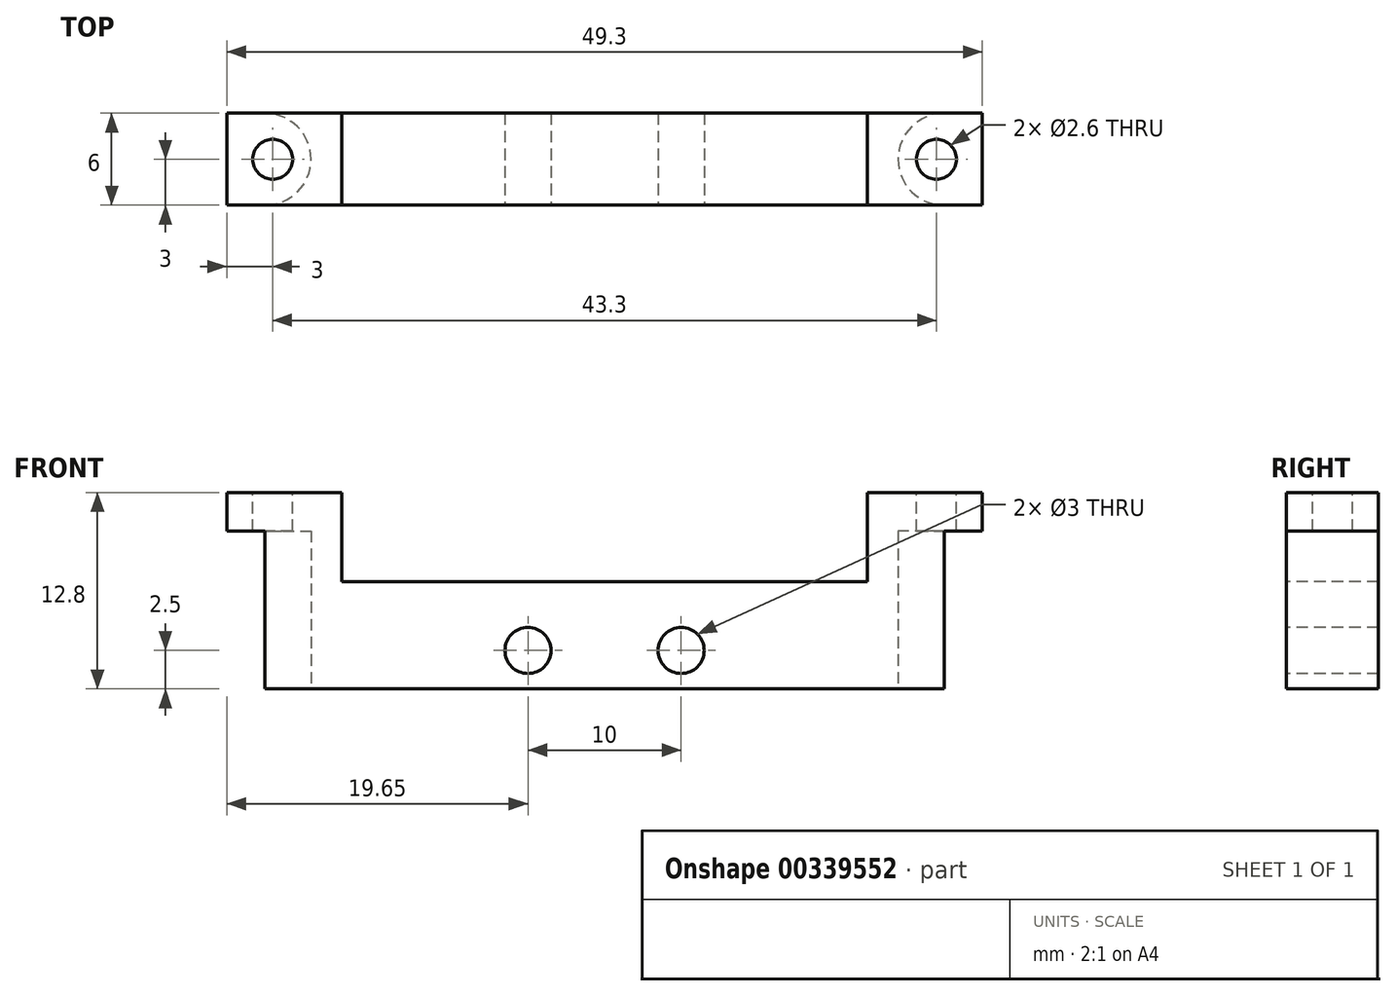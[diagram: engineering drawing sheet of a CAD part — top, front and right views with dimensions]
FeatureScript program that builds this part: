
annotation { "Feature Type Name" : "Feature", "Feature Type Description" : "" }
export const myFeature = defineFeature(function(context is Context, id is Id, definition is map)
    precondition{}
    {
        {
            var Q0;
            Q0=qCreatedBy(makeId("Top.planeOp"),FACE);
            var sketch = newSketch(context, id + "F0", { "sketchPlane" : qUnion([Q0])});
            skLineSegment(sketch, "E0.bottom", {"start": v(0, 3) * mm, "end": v(-24.65, 3) * mm});
            skLineSegment(sketch, "E0.top", {"start": v(0, -3) * mm, "end": v(-24.65, -3) * mm});
            skLineSegment(sketch, "E0.left", {"start": v(0, 3) * mm, "end": v(0, -3) * mm});
            skLineSegment(sketch, "E0.right", {"start": v(-24.65, 3) * mm, "end": v(-24.65, -3) * mm});
            skSolve(sketch);
        }
        {
            var Q0;
            Q0=makeQuery(id+"F0.imprint","IMPRINT",FACE,{"disambiguationData":[TD([[makeQuery(id+"F0.imprint","IMPRINT",EDGE,{"derivedFrom":sQuery(id+"F0.wireOp",EDGE,"E0.bottom")}),1.0]])]});
            extrude(context, id + "F1", {"entities" : qUnion([Q0]), "depth" : (10.3 + 2.5) * mm});
        }
        {
            var Q0;
            Q0=makeQuery(id+"F1.opExtrude","SWEPT_FACE",FACE,{"disambiguationData":[OSD([sQuery(id+"F0.wireOp",EDGE,"E0.top")])]});
            var sketch = newSketch(context, id + "F2", { "sketchPlane" : qUnion([Q0])});
            skLineSegment(sketch, "E1", {"start": v(-17.15, 12.8) * mm, "end": v(-17.15, 7) * mm});
            skLineSegment(sketch, "E2", {"start": v(-17.15, 7) * mm, "end": v(0, 7) * mm});
            skLineSegment(sketch, "E3", {"start": v(-17.15, 12.8) * mm, "end": v(0, 12.8) * mm});
            skLineSegment(sketch, "E4", {"start": v(0, 7) * mm, "end": v(0, 12.8) * mm});
            skSolve(sketch);
        }
        {
            var Q0;
            Q0=makeQuery(id+"F2.imprint","IMPRINT",FACE,{"disambiguationData":[TD([[makeQuery(id+"F2.imprint","IMPRINT",EDGE,{"derivedFrom":sQuery(id+"F2.wireOp",EDGE,"E1")}),1.0]])]});
            extrude(context, id + "F3", {"entities" : qUnion([Q0]), "operationType" : NewBodyOperationType.REMOVE, "oppositeDirection" : true, "depth" : 25 * mm});
        }
        {
            var Q0;
            Q0=makeQuery(id+"F1.opExtrude","CAP_FACE",FACE,{"disambiguationData":[OSD([sQuery(id+"F0.wireOp",EDGE,"E0.bottom"),sQuery(id+"F0.wireOp",EDGE,"E0.top"),sQuery(id+"F0.wireOp",EDGE,"E0.left"),sQuery(id+"F0.wireOp",EDGE,"E0.right")])],"isStart":false});
            var sketch = newSketch(context, id + "F4", { "sketchPlane" : qUnion([Q0])});
            skCircle(sketch, "E5", {"center": v(-21.65, 0) * mm, "radius": 1.3 * mm});
            skSolve(sketch);
        }
        {
            var Q0;
            Q0=makeQuery(id+"F1.opExtrude","CAP_FACE",FACE,{"disambiguationData":[OSD([sQuery(id+"F0.wireOp",EDGE,"E0.bottom"),sQuery(id+"F0.wireOp",EDGE,"E0.top"),sQuery(id+"F0.wireOp",EDGE,"E0.left"),sQuery(id+"F0.wireOp",EDGE,"E0.right")])],"isStart":true});
            var sketch = newSketch(context, id + "F5", { "sketchPlane" : qUnion([Q0])});
            skPoint(sketch, "E6.orphan", {"position": v(-24.65, -3) * mm});
            skPoint(sketch, "E7.orphan", {"position": v(-24.65, 3) * mm});
            skArc(sketch, "E8", {"start": v(-22.15, -3) * mm, "mid": v(-19.15, 0) * mm, "end": v(-22.15, 3) * mm});
            skLineSegment(sketch, "E9", {"start": v(-22.15, 3) * mm, "end": v(-22.15, 3) * mm});
            skLineSegment(sketch, "E10", {"start": v(-22.15, -3) * mm, "end": v(-24.65, -3) * mm});
            skLineSegment(sketch, "E11", {"start": v(-24.65, 3) * mm, "end": v(-22.15, 3) * mm});
            skLineSegment(sketch, "E12.trimOffspring", {"start": v(-22.15, -3) * mm, "end": v(-22.15, -3) * mm});
            skSolve(sketch);
        }
        {
            var Q0;
            Q0 = qSketchRegion(id + "F5", true);
            var Q1;
            Q1=makeQuery(id+"F5.imprint","IMPRINT",FACE,{"disambiguationData":[TD([[makeQuery(id+"F5.imprint","IMPRINT",EDGE,{"derivedFrom":sQuery(id+"F5.wireOp",EDGE,"E8")}),1.0]])]});
            extrude(context, id + "F6", {"entities" : qUnion([Q0, Q1]), "operationType" : NewBodyOperationType.REMOVE, "oppositeDirection" : true, "depth" : 10.3 * mm});
        }
        {
            var Q0;
            Q0=makeQuery(id+"F4.imprint","IMPRINT",FACE,{"disambiguationData":[TD([[makeQuery(id+"F4.imprint","IMPRINT",EDGE,{"derivedFrom":sQuery(id+"F4.wireOp",EDGE,"E5")}),1.0]])]});
            extrude(context, id + "F7", {"entities" : qUnion([Q0]), "operationType" : NewBodyOperationType.REMOVE, "oppositeDirection" : true, "depth" : 25 * mm});
        }
        {
            var Q0;
            Q0=makeQuery(id+"F1.opExtrude","SWEPT_FACE",FACE,{"disambiguationData":[OSD([sQuery(id+"F0.wireOp",EDGE,"E0.top")])]});
            var sketch = newSketch(context, id + "F8", { "sketchPlane" : qUnion([Q0])});
            skCircle(sketch, "E13", {"center": v(-5, 2.5) * mm, "radius": 1.5 * mm});
            skSolve(sketch);
        }
        {
            var Q0;
            Q0 = qSketchRegion(id + "F8", true);
            extrude(context, id + "F9", {"entities" : qUnion([Q0]), "operationType" : NewBodyOperationType.REMOVE, "oppositeDirection" : true, "depth" : 25 * mm});
        }
        {
            var Q0;
            Q0=makeQuery(id+"F1.opExtrude","SWEPT_BODY",BODY,{"disambiguationData":[OSD([sQuery(id+"F0.wireOp",EDGE,"E0.bottom"),sQuery(id+"F0.wireOp",EDGE,"E0.top"),sQuery(id+"F0.wireOp",EDGE,"E0.left"),sQuery(id+"F0.wireOp",EDGE,"E0.right")])]});
            var Q1;
            Q1=makeQuery(id+"F1.opExtrude","SWEPT_FACE",FACE,{"disambiguationData":[OSD([sQuery(id+"F0.wireOp",EDGE,"E0.left")])]});
            mirror(context, id + "F10", {"operationType" : NewBodyOperationType.ADD, "entities" : qUnion([Q0]), "mirrorPlane" : qUnion([Q1])});
        }
    });
